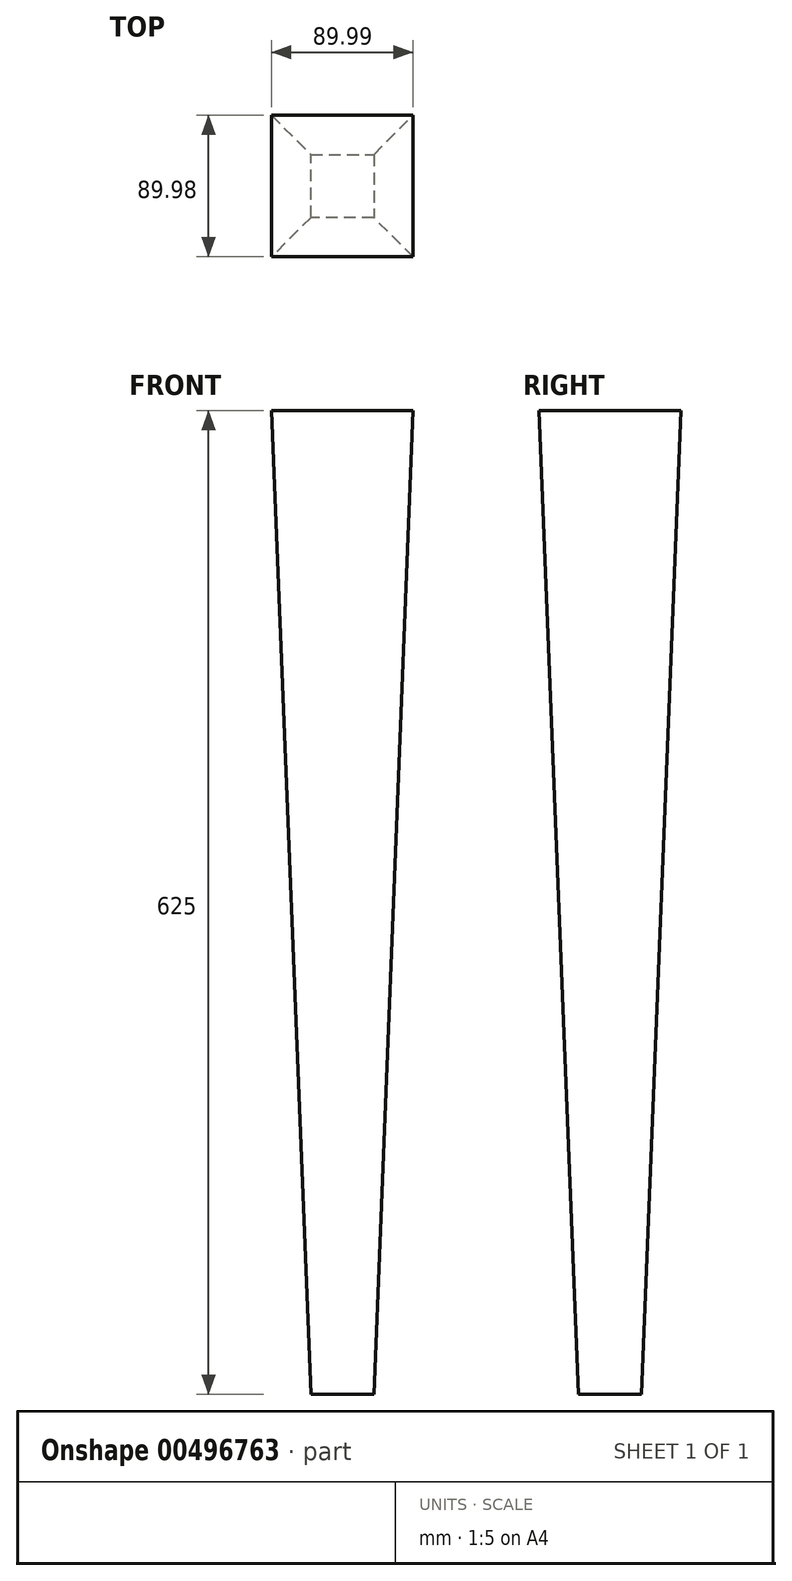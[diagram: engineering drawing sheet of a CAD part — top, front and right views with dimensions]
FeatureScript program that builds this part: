
annotation { "Feature Type Name" : "Feature", "Feature Type Description" : "" }
export const myFeature = defineFeature(function(context is Context, id is Id, definition is map)
    precondition{}
    {
        {
            var Q0;
            Q0=qCreatedBy(makeId("Top.planeOp"),FACE);
            var sketch = newSketch(context, id + "F0", { "sketchPlane" : qUnion([Q0])});
            skLineSegment(sketch, "E0.bottom", {"start": v(-9.02, -31.43) * mm, "end": v(30.98, -31.43) * mm});
            skLineSegment(sketch, "E0.top", {"start": v(-9.02, 8.57) * mm, "end": v(30.98, 8.57) * mm});
            skLineSegment(sketch, "E0.left", {"start": v(-9.02, -31.43) * mm, "end": v(-9.02, 8.57) * mm});
            skLineSegment(sketch, "E0.right", {"start": v(30.98, -31.43) * mm, "end": v(30.98, 8.57) * mm});
            skSolve(sketch);
        }
        {
            var Q0;
            Q0=makeQuery(id+"F0.imprint","IMPRINT",FACE,{"disambiguationData":[TD([[makeQuery(id+"F0.imprint","IMPRINT",EDGE,{"derivedFrom":sQuery(id+"F0.wireOp",EDGE,"E0.bottom")}),1.0]])]});
            extrude(context, id + "F1", {"entities" : qUnion([Q0]), "depth" : 625 * mm, "hasDraft" : true, "draftAngle" : 2.3 * degree});
        }
    });
